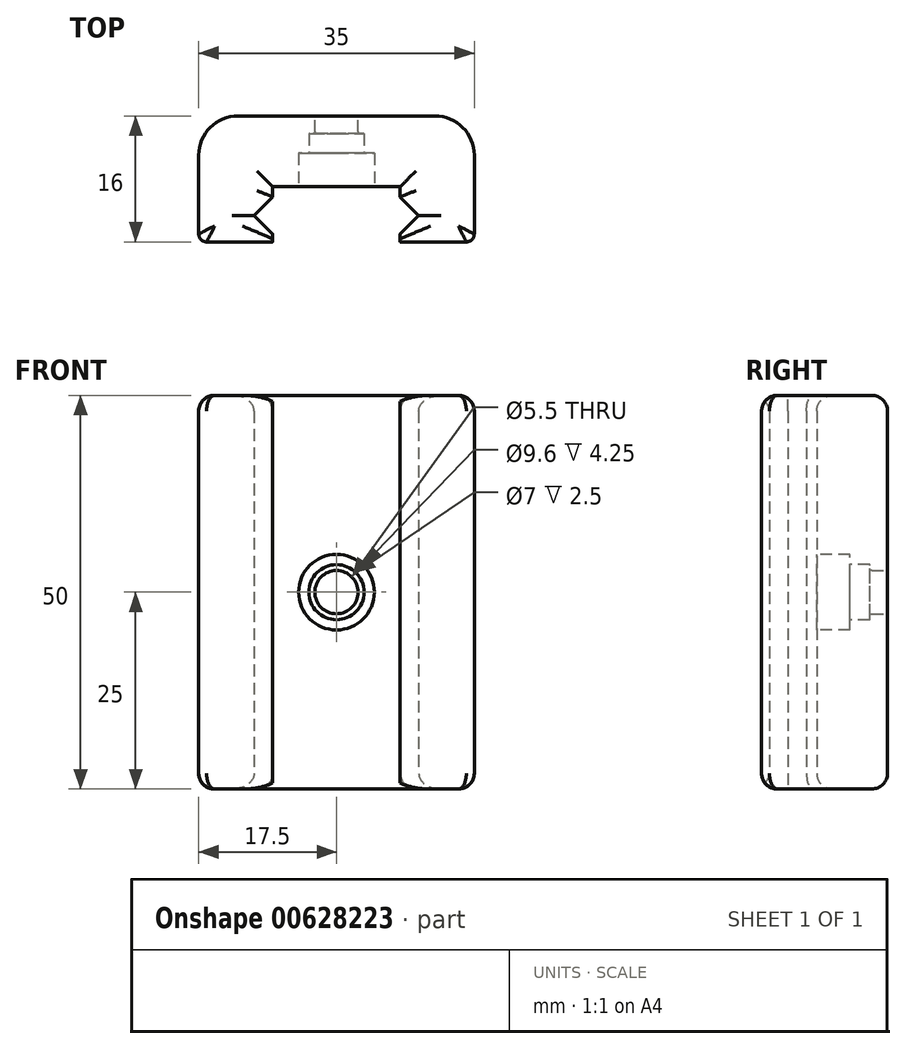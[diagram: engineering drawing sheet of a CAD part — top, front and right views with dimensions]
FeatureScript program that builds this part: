
annotation { "Feature Type Name" : "Feature", "Feature Type Description" : "" }
export const myFeature = defineFeature(function(context is Context, id is Id, definition is map)
    precondition{}
    {
        {
            var Q0;
            Q0=qCreatedBy(makeId("Top.planeOp"),FACE);
            var sketch = newSketch(context, id + "F0", { "sketchPlane" : qUnion([Q0])});
            skLineSegment(sketch, "E0", {"start": v(0, -5) * mm, "end": v(0, 0) * mm});
            skLineSegment(sketch, "E1.MirrorCS", {"start": v(8.1, -6.3) * mm, "end": v(8.1, -5) * mm});
            skLineSegment(sketch, "E2.MirrorCS", {"start": v(0, 0) * mm, "end": v(17.5, 0) * mm});
            skLineSegment(sketch, "E3.MirrorCS", {"start": v(17.5, 0) * mm, "end": v(17.5, -11) * mm});
            skLineSegment(sketch, "E4.MirrorCS", {"start": v(10.45, -8.65) * mm, "end": v(8.1, -6.3) * mm});
            skLineSegment(sketch, "E5.MirrorCS", {"start": v(8.1, -5) * mm, "end": v(0, -5) * mm});
            skLineSegment(sketch, "E6.MirrorCS", {"start": v(8.1, -11) * mm, "end": v(10.45, -8.65) * mm});
            skLineSegment(sketch, "E7", {"start": v(8.1, -11) * mm, "end": v(8.1, -12) * mm});
            skLineSegment(sketch, "E8", {"start": v(8.1, -12) * mm, "end": v(17.5, -12) * mm});
            skLineSegment(sketch, "E9", {"start": v(17.5, -12) * mm, "end": v(17.5, -11) * mm});
            skLineSegment(sketch, "E10.MirrorCS", {"start": v(-17.5, -12) * mm, "end": v(-17.5, -11) * mm});
            skLineSegment(sketch, "E11.MirrorCS", {"start": v(-8.1, -11) * mm, "end": v(-8.1, -12) * mm});
            skLineSegment(sketch, "E12.MirrorCS", {"start": v(0, 0) * mm, "end": v(-17.5, 0) * mm});
            skLineSegment(sketch, "E13.MirrorCS", {"start": v(-17.5, 0) * mm, "end": v(-17.5, -11) * mm});
            skLineSegment(sketch, "E14.MirrorCS", {"start": v(-8.1, -6.3) * mm, "end": v(-8.1, -5) * mm});
            skLineSegment(sketch, "E15.MirrorCS", {"start": v(-8.1, -5) * mm, "end": v(0, -5) * mm});
            skLineSegment(sketch, "E16.MirrorCS", {"start": v(-8.1, -12) * mm, "end": v(-17.5, -12) * mm});
            skLineSegment(sketch, "E17.MirrorCS", {"start": v(-8.1, -11) * mm, "end": v(-10.45, -8.65) * mm});
            skLineSegment(sketch, "E18.MirrorCS", {"start": v(-10.45, -8.65) * mm, "end": v(-8.1, -6.3) * mm});
            skSolve(sketch);
        }
        {
            var Q0;
            Q0 = qSketchRegion(id + "F0", true);
            extrude(context, id + "F1", {"entities" : qUnion([Q0]), "endBound" : BoundingType.SYMMETRIC, "depth" : 50 * mm, "offsetDistance" : 25 * mm});
        }
        {
            var Q0;
            Q0=makeQuery(id+"F1.opExtrude","SWEPT_FACE",FACE,{"disambiguationData":[OSD([sQuery(id+"F0.wireOp",EDGE,"E2.MirrorCS"),sQuery(id+"F0.wireOp",EDGE,"E12.MirrorCS")])]});
            var sketch = newSketch(context, id + "F2", { "sketchPlane" : qUnion([Q0])});
            skCircle(sketch, "E19", {"center": v(0, 0) * mm, "radius": 2.75 * mm});
            skSolve(sketch);
        }
        {
            var Q0;
            Q0 = qSketchRegion(id + "F2", true);
            extrude(context, id + "F3", {"entities" : qUnion([Q0]), "operationType" : NewBodyOperationType.REMOVE, "endBound" : BoundingType.THROUGH_ALL, "oppositeDirection" : true, "depth" : 25 * mm, "offsetDistance" : 25 * mm});
        }
        {
            var Q0;
            Q0=makeQuery(id+"F1.opExtrude","SWEPT_FACE",FACE,{"disambiguationData":[OSD([sQuery(id+"F0.wireOp",EDGE,"E2.MirrorCS"),sQuery(id+"F0.wireOp",EDGE,"E12.MirrorCS")])]});
            extrude(context, id + "F4", {"entities" : qUnion([Q0]), "operationType" : NewBodyOperationType.ADD, "depth" : 4 * mm, "offsetDistance" : 25 * mm});
        }
        {
            var Q0;
            Q0=makeQuery(id+"F1.opExtrude","SWEPT_FACE",FACE,{"disambiguationData":[OSD([sQuery(id+"F0.wireOp",EDGE,"E5.MirrorCS"),sQuery(id+"F0.wireOp",EDGE,"E15.MirrorCS")])]});
            var sketch = newSketch(context, id + "F5", { "sketchPlane" : qUnion([Q0])});
            skCircle(sketch, "E20", {"center": v(0, 0) * mm, "radius": 4.8 * mm});
            skSolve(sketch);
        }
        {
            var Q0;
            Q0 = qSketchRegion(id + "F5", true);
            extrude(context, id + "F6", {"entities" : qUnion([Q0]), "operationType" : NewBodyOperationType.REMOVE, "oppositeDirection" : true, "depth" : 4.25 * mm, "offsetDistance" : 25 * mm});
        }
        {
            var Q0;
            Q0=makeQuery(id+"F6.boolean.opBoolean","COPY",FACE,{"derivedFrom":makeQuery(id+"F6.opExtrude","CAP_FACE",FACE,{"disambiguationData":[OSD([sQuery(id+"F5.wireOp",EDGE,"E20")])],"isStart":false})});
            var sketch = newSketch(context, id + "F7", { "sketchPlane" : qUnion([Q0])});
            skCircle(sketch, "E21", {"center": v(0, 0) * mm, "radius": 3.5 * mm});
            skSolve(sketch);
        }
        {
            var Q0;
            Q0 = qSketchRegion(id + "F7", true);
            extrude(context, id + "F8", {"entities" : qUnion([Q0]), "operationType" : NewBodyOperationType.REMOVE, "oppositeDirection" : true, "depth" : 2.5 * mm, "offsetDistance" : 25 * mm});
        }
        {
            var Q0;
            Q0=makeQuery(id+"F6.boolean.opBoolean","COPY",EDGE,{"derivedFrom":makeQuery(id+"F6.opExtrude","CAP_EDGE",EDGE,{"disambiguationData":[OSD([sQuery(id+"F5.wireOp",EDGE,"E20")])],"isStart":true})});
            var Q1;
            Q1=makeQuery(id+"F8.boolean.opBoolean","COPY",EDGE,{"derivedFrom":makeQuery(id+"F8.opExtrude","CAP_EDGE",EDGE,{"disambiguationData":[OSD([sQuery(id+"F7.wireOp",EDGE,"E21")])],"isStart":true})});
            var Q2;
            {var subQ0=sQuery(id+"F2.wireOp",EDGE,"E19");Q2=makeQuery(id+"F8.boolean.opBoolean","INTERSECT",EDGE,{"derivedFrom":[makeQuery(id+"F4.boolean.opBoolean","MERGE",FACE,{"derivedFrom":[makeQuery(id+"F3.boolean.opBoolean","COPY",FACE,{"derivedFrom":makeQuery(id+"F3.opExtrude","SWEPT_FACE",FACE,{"disambiguationData":[OSD([subQ0])]})}),makeQuery(id+"F4.opExtrude","SWEPT_FACE",FACE,{"disambiguationData":[OSD([subQ0])]})]}),makeQuery(id+"F8.opExtrude","CAP_FACE",FACE,{"disambiguationData":[OSD([sQuery(id+"F7.wireOp",EDGE,"E21")])],"isStart":false})]});}
            fillet(context, id + "F9", {"entities" : qUnion([Q0, Q1, Q2]), "radius" : .25 * mm, "tangentPropagation" : true, "allowEdgeOverflow" : false});
        }
        {
            var Q0;
            {var subQ0=sQuery(id+"F0.wireOp",EDGE,"E12.MirrorCS");var subQ1=sQuery(id+"F0.wireOp",EDGE,"E2.MirrorCS");Q0=makeQuery(id+"F4.boolean.opBoolean","MERGE",FACE,{"derivedFrom":[makeQuery(id+"F1.opExtrude","CAP_FACE",FACE,{"disambiguationData":[OSD([sQuery(id+"F0.wireOp",EDGE,"E1.MirrorCS"),subQ1,sQuery(id+"F0.wireOp",EDGE,"E3.MirrorCS"),sQuery(id+"F0.wireOp",EDGE,"E4.MirrorCS"),sQuery(id+"F0.wireOp",EDGE,"E5.MirrorCS"),sQuery(id+"F0.wireOp",EDGE,"E6.MirrorCS"),sQuery(id+"F0.wireOp",EDGE,"E7"),sQuery(id+"F0.wireOp",EDGE,"E8"),sQuery(id+"F0.wireOp",EDGE,"E9"),sQuery(id+"F0.wireOp",EDGE,"E10.MirrorCS"),sQuery(id+"F0.wireOp",EDGE,"E11.MirrorCS"),subQ0,sQuery(id+"F0.wireOp",EDGE,"E13.MirrorCS"),sQuery(id+"F0.wireOp",EDGE,"E14.MirrorCS"),sQuery(id+"F0.wireOp",EDGE,"E15.MirrorCS"),sQuery(id+"F0.wireOp",EDGE,"E16.MirrorCS"),sQuery(id+"F0.wireOp",EDGE,"E17.MirrorCS"),sQuery(id+"F0.wireOp",EDGE,"E18.MirrorCS")])],"isStart":false}),makeQuery(id+"F4.opExtrude","SWEPT_FACE",FACE,{"disambiguationData":[OSD([subQ1,subQ0]),TDD([makeQuery(id+"F1.opExtrude","CAP_EDGE",EDGE,{"disambiguationData":[OSD([subQ1,subQ0])],"isStart":false})])]})]});}
            var Q1;
            {var subQ0=sQuery(id+"F0.wireOp",EDGE,"E12.MirrorCS");var subQ1=sQuery(id+"F0.wireOp",EDGE,"E2.MirrorCS");Q1=makeQuery(id+"F4.boolean.opBoolean","MERGE",FACE,{"derivedFrom":[makeQuery(id+"F1.opExtrude","CAP_FACE",FACE,{"disambiguationData":[OSD([sQuery(id+"F0.wireOp",EDGE,"E1.MirrorCS"),subQ1,sQuery(id+"F0.wireOp",EDGE,"E3.MirrorCS"),sQuery(id+"F0.wireOp",EDGE,"E4.MirrorCS"),sQuery(id+"F0.wireOp",EDGE,"E5.MirrorCS"),sQuery(id+"F0.wireOp",EDGE,"E6.MirrorCS"),sQuery(id+"F0.wireOp",EDGE,"E7"),sQuery(id+"F0.wireOp",EDGE,"E8"),sQuery(id+"F0.wireOp",EDGE,"E9"),sQuery(id+"F0.wireOp",EDGE,"E10.MirrorCS"),sQuery(id+"F0.wireOp",EDGE,"E11.MirrorCS"),subQ0,sQuery(id+"F0.wireOp",EDGE,"E13.MirrorCS"),sQuery(id+"F0.wireOp",EDGE,"E14.MirrorCS"),sQuery(id+"F0.wireOp",EDGE,"E15.MirrorCS"),sQuery(id+"F0.wireOp",EDGE,"E16.MirrorCS"),sQuery(id+"F0.wireOp",EDGE,"E17.MirrorCS"),sQuery(id+"F0.wireOp",EDGE,"E18.MirrorCS")])],"isStart":true}),makeQuery(id+"F4.opExtrude","SWEPT_FACE",FACE,{"disambiguationData":[OSD([subQ1,subQ0]),TDD([makeQuery(id+"F1.opExtrude","CAP_EDGE",EDGE,{"disambiguationData":[OSD([subQ1,subQ0])],"isStart":true})])]})]});}
            fillet(context, id + "F10", {"entities" : qUnion([Q0, Q1]), "radius" : 2 * mm, "tangentPropagation" : true, "allowEdgeOverflow" : false});
        }
        {
            var Q0;
            Q0=makeQuery(id+"F4.opExtrude","CAP_EDGE",EDGE,{"disambiguationData":[OSD([sQuery(id+"F0.wireOp",EDGE,"E12.MirrorCS"),sQuery(id+"F0.wireOp",EDGE,"E13.MirrorCS")])],"isStart":false});
            var Q1;
            Q1=makeQuery(id+"F4.opExtrude","CAP_EDGE",EDGE,{"disambiguationData":[OSD([sQuery(id+"F0.wireOp",EDGE,"E2.MirrorCS"),sQuery(id+"F0.wireOp",EDGE,"E3.MirrorCS")])],"isStart":false});
            fillet(context, id + "F11", {"entities" : qUnion([Q0, Q1]), "radius" : 5 * mm, "tangentPropagation" : true, "allowEdgeOverflow" : false});
        }
        {
            var Q0;
            Q0=makeQuery(id+"F1.opExtrude","SWEPT_EDGE",EDGE,{"disambiguationData":[OSD([sQuery(id+"F0.wireOp",EDGE,"E8"),sQuery(id+"F0.wireOp",EDGE,"E9")])]});
            var Q1;
            Q1=makeQuery(id+"F1.opExtrude","SWEPT_EDGE",EDGE,{"disambiguationData":[OSD([sQuery(id+"F0.wireOp",EDGE,"E10.MirrorCS"),sQuery(id+"F0.wireOp",EDGE,"E16.MirrorCS")])]});
            fillet(context, id + "F12", {"entities" : qUnion([Q0, Q1]), "radius" : 1 * mm, "tangentPropagation" : true, "allowEdgeOverflow" : false});
        }
    });
